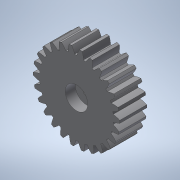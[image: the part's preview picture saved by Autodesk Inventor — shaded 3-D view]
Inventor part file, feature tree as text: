
AUTODESK INVENTOR PART (.ipt)
format: ipt  version: 2020 (Build 240168000, 168)  size: 318,464 bytes
history: native  units: mm
features: other x9, extrude x4, reference x4, sketch x3
ambient origin geometry x8: Origin, YZ Plane, XZ Plane, XY Plane, X Axis, Y Axis, Z Axis, Center Point
bodies: Body1 (feature_tree)
feature tree (20):
  other  "Bryła1"
  sketch  "Szkic1"
  extrude  "Wyciągnięcie proste1"  Depth=30.0mm
  extrude  "Wyciągnięcie proste2"  Depth=3.0mm TaperAngle=0.0deg
  extrude  "Wyciągnięcie proste3"  Depth=0.25mm
  extrude  "Wyciągnięcie proste5"  Depth=1.5mm TaperAngle=0.0deg
  reference  "Odniesienie1"
  reference  "Odniesienie2"
  reference  "Odniesienie3"
  sketch  "Szkic2"
  sketch  "Szkic4"
  reference  "Odniesienie4"
  other  "<userpath>\Desktop\3d\scanning-robot\Assembly1.iam"
  other  "Assembly1.iam"
  other  "Tower Pro MG90S Micro servo:2"
  other  "Цилиндрическое зубчатое зацепление:5"
  other  "Цилиндрическое зубчатое зацепление2:1"
  other  "<userpath>\Desktop\ScanBot\3d-model\Assembly1.iam"
  other  "Przekładnie walcowe:2"
  other  "Przekładnia walcowa2:1"
